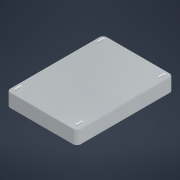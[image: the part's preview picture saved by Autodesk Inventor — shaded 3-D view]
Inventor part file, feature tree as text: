
AUTODESK INVENTOR PART (.ipt)
format: ipt  version: 2021 (Build 250183000, 183)  size: 158,720 bytes
history: native  units: mm
features: extrude x2, fillet x2, sketch x2, other x1
ambient origin geometry x8: Origin, YZ Plane, XZ Plane, XY Plane, X Axis, Y Axis, Z Axis, Center Point
bodies: Body1 (feature_tree)
feature tree (7):
  other  "ソリッド1"
  extrude  "押し出し1"  Depth=170.0mm
  fillet  "フィレット1"  Radius=233.0mm
  fillet  "フィレット2"  Radius=34.0mm
  extrude  "押し出し2"  Depth=10.0mm
  sketch  "スケッチ2"
  sketch  "スケッチ3"
